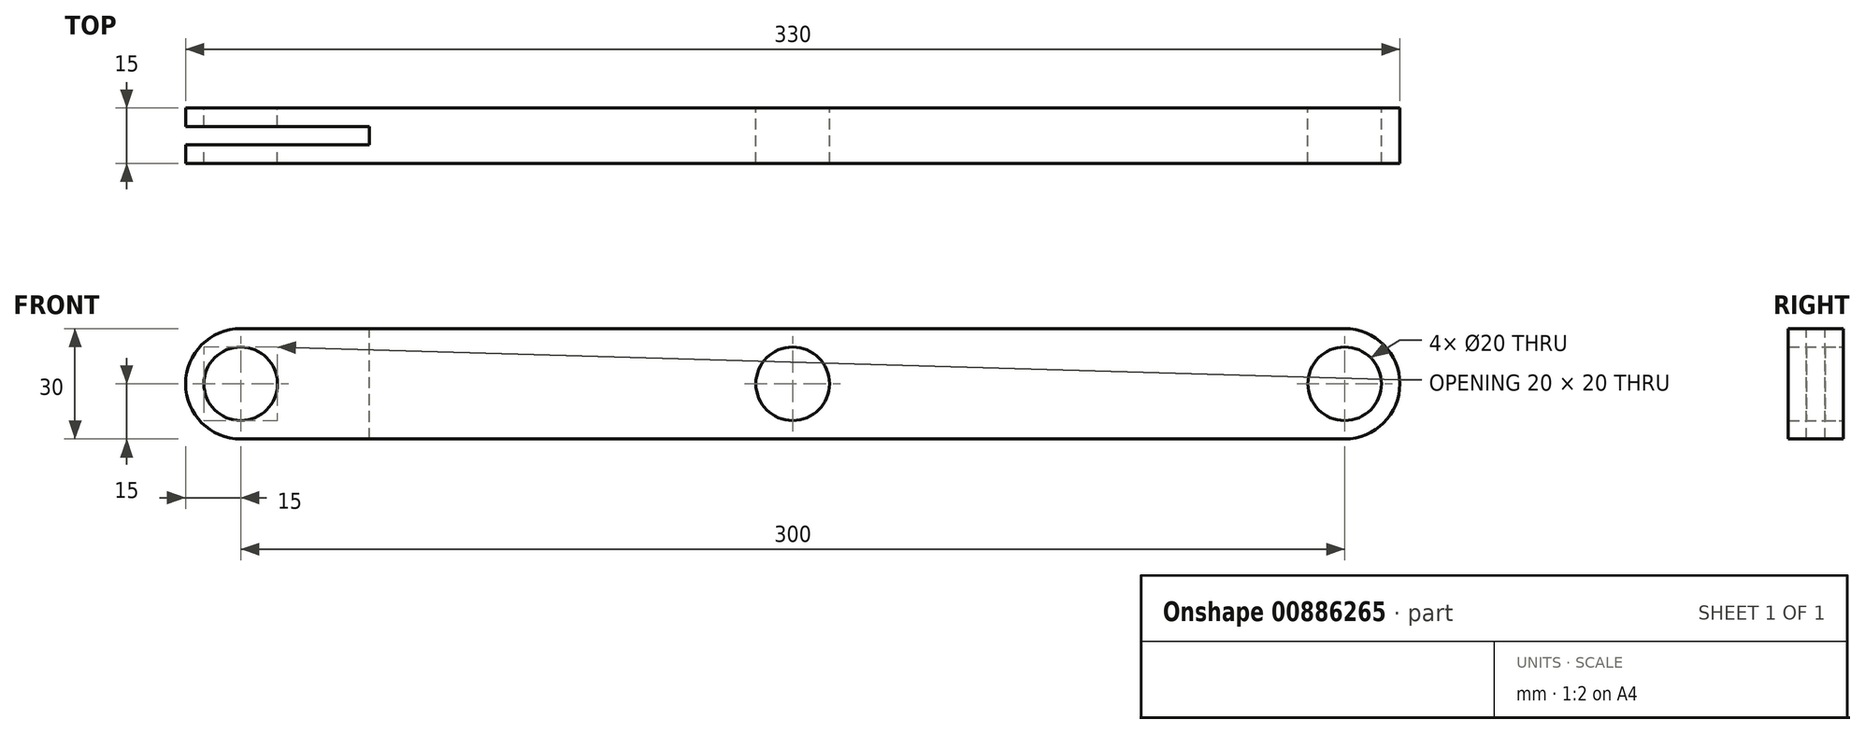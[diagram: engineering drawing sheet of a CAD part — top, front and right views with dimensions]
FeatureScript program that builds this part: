
annotation { "Feature Type Name" : "Feature", "Feature Type Description" : "" }
export const myFeature = defineFeature(function(context is Context, id is Id, definition is map)
    precondition{}
    {
        {
            var Q0;
            Q0=qCreatedBy(makeId("Front.planeOp"),FACE);
            var sketch = newSketch(context, id + "F0", { "sketchPlane" : qUnion([Q0])});
            skLineSegment(sketch, "E0.bottom", {"start": v(-150, 15) * mm, "end": v(150, 15) * mm});
            skLineSegment(sketch, "E0.top", {"start": v(-150, -15) * mm, "end": v(150, -15) * mm});
            skLineSegment(sketch, "E0.left", {"start": v(-150, 15) * mm, "end": v(-150, -15) * mm});
            skLineSegment(sketch, "E0.right", {"start": v(150, 15) * mm, "end": v(150, -15) * mm});
            skPoint(sketch, "E0.middle", {"position": v(0, 0) * mm});
            skArc(sketch, "E1", {"start": v(-150, 15) * mm, "mid": v(-165, 0) * mm, "end": v(-150, -15) * mm});
            skArc(sketch, "E2", {"start": v(150, 15) * mm, "mid": v(165, 0) * mm, "end": v(150, -15) * mm});
            skCircle(sketch, "E3", {"center": v(-150, 0) * mm, "radius": 10 * mm});
            skCircle(sketch, "E4", {"center": v(150, 0) * mm, "radius": 10 * mm});
            skCircle(sketch, "E5", {"center": v(0, 0) * mm, "radius": 10 * mm});
            skSolve(sketch);
        }
        {
            var Q0;
            Q0 = qSketchRegion(id + "F0", true);
            extrude(context, id + "F1", {"entities" : qUnion([Q0]), "depth" : 15 * mm, "offsetDistance" : 25 * mm, "symmetric" : true});
        }
        {
            var Q0;
            Q0=qCreatedBy(makeId("Top.planeOp"),FACE);
            var sketch = newSketch(context, id + "F2", { "sketchPlane" : qUnion([Q0])});
            skLineSegment(sketch, "E6.bottom", {"start": v(-115, -2.5) * mm, "end": v(-165, -2.5) * mm});
            skLineSegment(sketch, "E6.top", {"start": v(-115, 2.5) * mm, "end": v(-165, 2.5) * mm});
            skLineSegment(sketch, "E6.left", {"start": v(-115, -2.5) * mm, "end": v(-115, 2.5) * mm});
            skLineSegment(sketch, "E6.right", {"start": v(-165, -2.5) * mm, "end": v(-165, 2.5) * mm});
            skPoint(sketch, "E6.middle", {"position": v(-140, 0) * mm});
            skSolve(sketch);
        }
        {
            var Q0;
            Q0 = qSketchRegion(id + "F2", true);
            extrude(context, id + "F3", {"entities" : qUnion([Q0]), "operationType" : NewBodyOperationType.REMOVE, "oppositeDirection" : true, "depth" : 30 * mm, "offsetDistance" : 25 * mm, "symmetric" : true});
        }
    });
